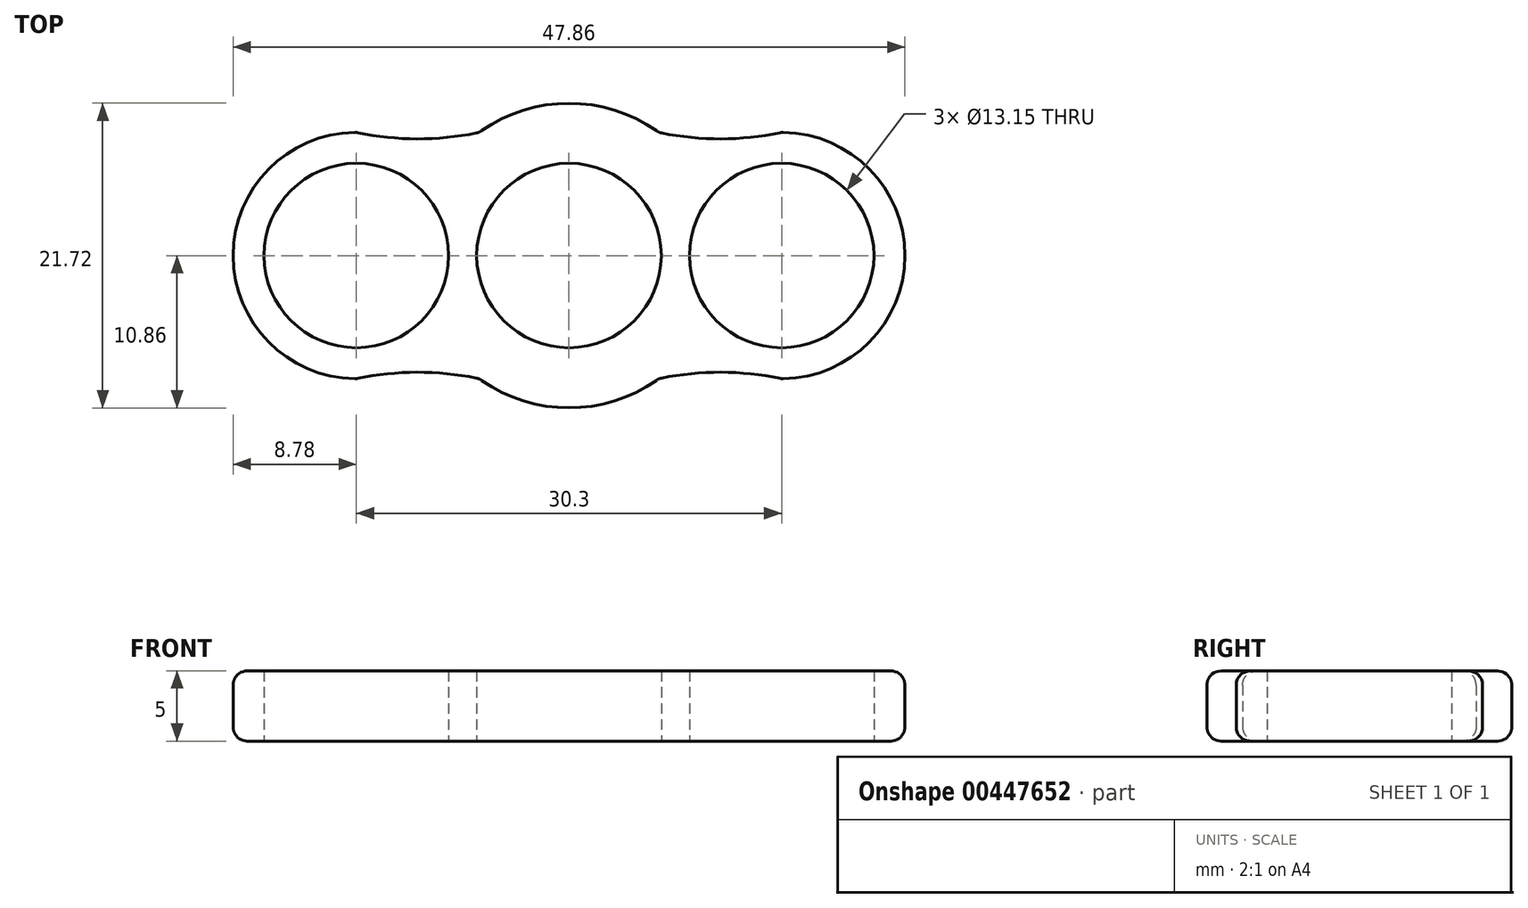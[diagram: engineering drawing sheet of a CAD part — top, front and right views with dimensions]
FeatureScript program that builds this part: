
annotation { "Feature Type Name" : "Feature", "Feature Type Description" : "" }
export const myFeature = defineFeature(function(context is Context, id is Id, definition is map)
    precondition{}
    {
        {
            var Q0;
            Q0=qCreatedBy(makeId("Top.planeOp"),FACE);
            var sketch = newSketch(context, id + "F0", { "sketchPlane" : qUnion([Q0])});
            skCircle(sketch, "E0", {"center": v(0, 0) * mm, "radius": 6.58 * mm});
            skCircle(sketch, "E1", {"center": v(-15.15, 0) * mm, "radius": 6.58 * mm});
            skCircle(sketch, "E2", {"center": v(15.15, 0) * mm, "radius": 6.58 * mm});
            skPoint(sketch, "E3", {"position": v(-8.57, 0) * mm});
            skPoint(sketch, "E4", {"position": v(-6.58, 0) * mm});
            skPoint(sketch, "E5", {"position": v(6.58, 0) * mm});
            skPoint(sketch, "E6", {"position": v(8.57, 0) * mm});
            skLineSegment(sketch, "E7", {"start": v(-8.57, 0) * mm, "end": v(-6.58, 0) * mm, "construction": true});
            skLineSegment(sketch, "E8", {"start": v(6.58, 0) * mm, "end": v(8.57, 0) * mm});
            skArc(sketch, "E9", {"start": v(-15.15, 8.78) * mm, "mid": v(-23.93, 0) * mm, "end": v(-15.15, -8.78) * mm});
            skArc(sketch, "E10", {"start": v(15.15, 8.78) * mm, "mid": v(23.93, 0) * mm, "end": v(15.15, -8.78) * mm});
            skArc(sketch, "E11", {"start": v(6.39, 8.78) * mm, "mid": v(0, 10.86) * mm, "end": v(-6.39, 8.78) * mm});
            skArc(sketch, "E12", {"start": v(6.39, -8.78) * mm, "mid": v(0, -10.86) * mm, "end": v(-6.39, -8.78) * mm});
            skArc(sketch, "E13", {"start": v(-15.15, 8.78) * mm, "mid": v(-10.77, 8.32) * mm, "end": v(-6.39, 8.78) * mm});
            skArc(sketch, "E14", {"start": v(6.39, 8.78) * mm, "mid": v(10.77, 8.32) * mm, "end": v(15.15, 8.78) * mm});
            skArc(sketch, "E15", {"start": v(-6.39, -8.78) * mm, "mid": v(-10.77, -8.32) * mm, "end": v(-15.15, -8.78) * mm});
            skArc(sketch, "E16", {"start": v(15.15, -8.78) * mm, "mid": v(10.77, -8.32) * mm, "end": v(6.39, -8.78) * mm});
            skLineSegment(sketch, "E17", {"start": v(-15.15, -8.78) * mm, "end": v(-6.39, -8.78) * mm, "construction": true});
            skLineSegment(sketch, "E18", {"start": v(6.39, -8.78) * mm, "end": v(15.15, -8.78) * mm, "construction": true});
            skLineSegment(sketch, "E19", {"start": v(6.39, 8.78) * mm, "end": v(15.15, 8.78) * mm, "construction": true});
            skLineSegment(sketch, "E20", {"start": v(-15.15, 8.78) * mm, "end": v(-6.39, 8.78) * mm, "construction": true});
            skLineSegment(sketch, "E21", {"start": v(15.15, 8.78) * mm, "end": v(10.77, 29.46) * mm, "construction": true});
            skLineSegment(sketch, "E22", {"start": v(-15.15, 8.78) * mm, "end": v(-10.77, 29.46) * mm, "construction": true});
            skLineSegment(sketch, "E23", {"start": v(-15.15, -8.78) * mm, "end": v(-10.77, -29.46) * mm, "construction": true});
            skLineSegment(sketch, "E24", {"start": v(15.15, -8.78) * mm, "end": v(10.77, -29.46) * mm, "construction": true});
            skSolve(sketch);
        }
        {
            var Q0;
            Q0=makeQuery(id+"F0.imprint","IMPRINT",FACE,{"disambiguationData":[TD([[makeQuery(id+"F0.imprint","IMPRINT",EDGE,{"derivedFrom":sQuery(id+"F0.wireOp",EDGE,"E0")}),-1.0]])]});
            extrude(context, id + "F1", {"entities" : qUnion([Q0]), "depth" : 5 * mm, "offsetDistance" : 25.4 * mm});
        }
        {
            var Q0;
            Q0=makeQuery(id+"F1.opExtrude","SWEPT_FACE",FACE,{"disambiguationData":[OSD([sQuery(id+"F0.wireOp",EDGE,"E9")])]});
            var Q1;
            Q1=makeQuery(id+"F1.opExtrude","SWEPT_FACE",FACE,{"disambiguationData":[OSD([sQuery(id+"F0.wireOp",EDGE,"E15")])]});
            var Q2;
            Q2=makeQuery(id+"F1.opExtrude","SWEPT_FACE",FACE,{"disambiguationData":[OSD([sQuery(id+"F0.wireOp",EDGE,"E12")])]});
            var Q3;
            Q3=makeQuery(id+"F1.opExtrude","SWEPT_FACE",FACE,{"disambiguationData":[OSD([sQuery(id+"F0.wireOp",EDGE,"E16")])]});
            var Q4;
            Q4=makeQuery(id+"F1.opExtrude","SWEPT_FACE",FACE,{"disambiguationData":[OSD([sQuery(id+"F0.wireOp",EDGE,"E10")])]});
            var Q5;
            Q5=makeQuery(id+"F1.opExtrude","SWEPT_FACE",FACE,{"disambiguationData":[OSD([sQuery(id+"F0.wireOp",EDGE,"E14")])]});
            var Q6;
            Q6=makeQuery(id+"F1.opExtrude","SWEPT_FACE",FACE,{"disambiguationData":[OSD([sQuery(id+"F0.wireOp",EDGE,"E11")])]});
            var Q7;
            Q7=makeQuery(id+"F1.opExtrude","SWEPT_FACE",FACE,{"disambiguationData":[OSD([sQuery(id+"F0.wireOp",EDGE,"E13")])]});
            fillet(context, id + "F2", {"entities" : qUnion([Q0, Q1, Q2, Q3, Q4, Q5, Q6, Q7]), "radius" : 1 * mm, "tangentPropagation" : true, "allowEdgeOverflow" : false});
        }
    });
